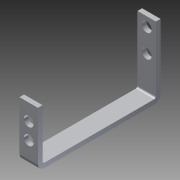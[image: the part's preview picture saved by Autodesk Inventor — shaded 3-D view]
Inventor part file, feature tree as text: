
AUTODESK INVENTOR PART (.ipt)
format: ipt  version: 2013 (Build 170138000, 138)  size: 215,552 bytes
history: native  units: in
note: dims shown in document units (in); Inventor stores cm internally (conversion verified against a paired STEP export)
features: other x8, sheet_metal_op x7, sketch x6, reference x2
ambient origin geometry x8: Origin, YZ Plane, XZ Plane, XY Plane, X Axis, Y Axis, Z Axis, Center Point
bodies: Solid1 (feature_tree)
feature tree (23):
  sheet_metal_op  "Face1"
  sheet_metal_op  "Flange1"
  sheet_metal_op  "Flange2"
  sketch  "Sketch1"  dims[d0=0.5in]
  other  "Plate1"
  sketch  "Sketch2"  dims[d1=1.75in]
  other  "Plate2"
  sheet_metal_op  "Bend1"
  sheet_metal_op  "Corner1"
  sketch  "Sketch3"  dims[d2=0.125in]
  reference  "Reference1"
  reference  "Reference2"
  sketch  "Sketch5"  dims[d4=0.0625in]
  other  "Plate3"
  sheet_metal_op  "Bend2"
  sheet_metal_op  "Corner2"
  sketch  "Sketch6"  dims[d5=0.25in d6=0.125in d7=3.1473in d8=90.0deg d9=0.05in d10=0.5in d11=0.125in d12=0.125in d13=0.125in d14=0.0in d19=0.125in d20=0.0625in d21=0.25in d22=0.125in d23=1.5in d24=90.0deg d25=0.05in d26=0.5in d27=0.125in d28=0.125in d29=0.4417in d31=0.442in d32=0.266in d33=0.266in d34=0.125in d35=0.0in d15=0.0625in d16=0.125in d17=0.0in d18=0.125in]
  other  "Cut1"
  other  "Cut3"
  other  "Definition1"
  sketch  "Sketch4"  dims[d3=0.125in]
  other  "Cut2"
  other  "Cut4"
